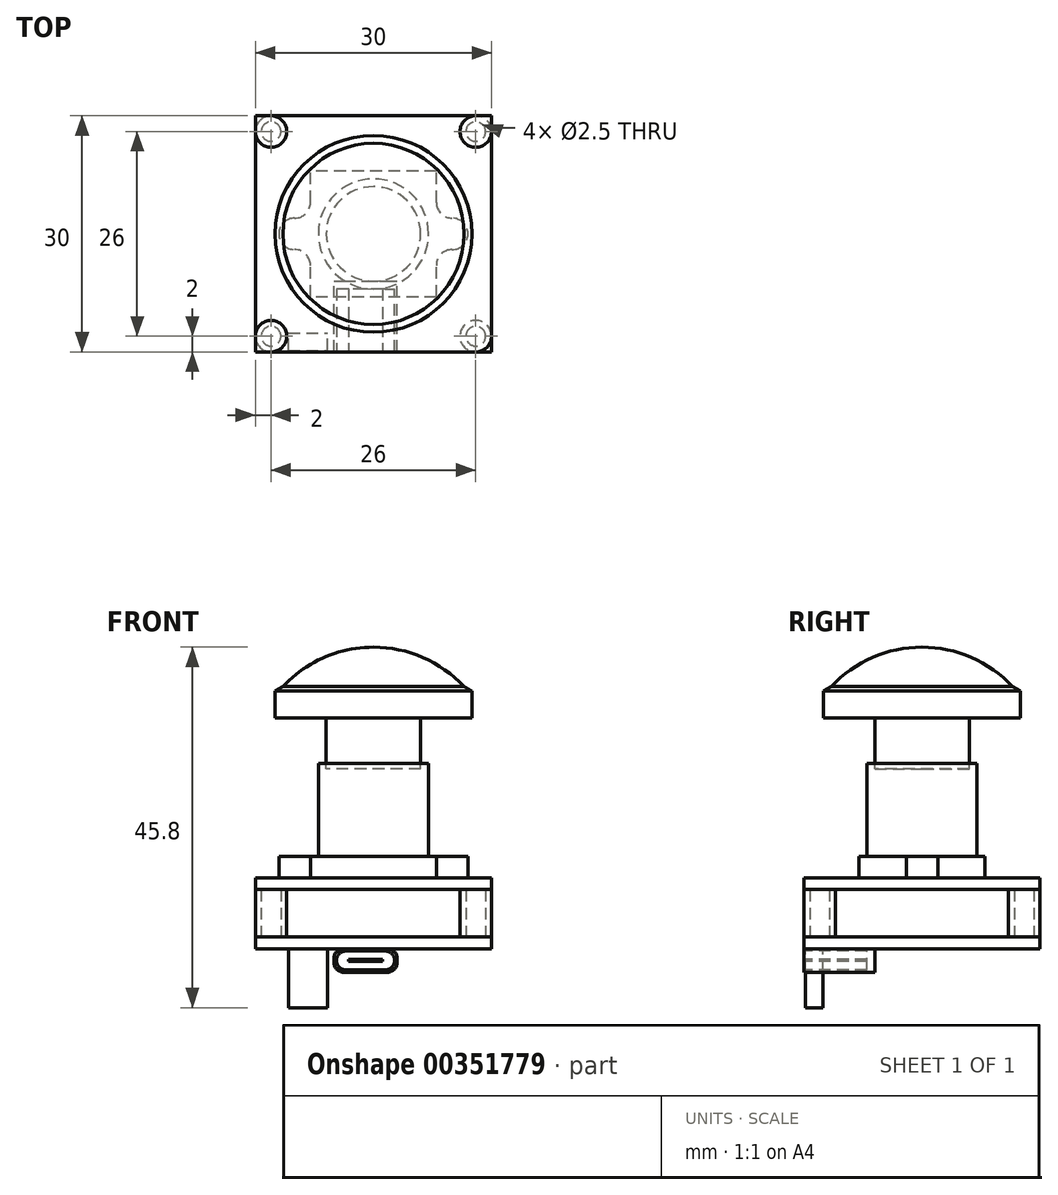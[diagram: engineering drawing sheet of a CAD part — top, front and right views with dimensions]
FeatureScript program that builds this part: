
annotation { "Feature Type Name" : "Feature", "Feature Type Description" : "" }
export const myFeature = defineFeature(function(context is Context, id is Id, definition is map)
    precondition{}
    {
        {
            var Q0;
            Q0=qCreatedBy(makeId("Top.planeOp"),FACE);
            var sketch = newSketch(context, id + "F0", { "sketchPlane" : qUnion([Q0])});
            skLineSegment(sketch, "E0.bottom", {"start": v(15, -15) * mm, "end": v(-15, -15) * mm});
            skLineSegment(sketch, "E0.top", {"start": v(15, 15) * mm, "end": v(-15, 15) * mm});
            skLineSegment(sketch, "E0.left", {"start": v(15, -15) * mm, "end": v(15, 15) * mm});
            skLineSegment(sketch, "E0.right", {"start": v(-15, -15) * mm, "end": v(-15, 15) * mm});
            skPoint(sketch, "E0.middle", {"position": v(0, 0) * mm});
            skSolve(sketch);
        }
        {
            var Q0;
            Q0=makeQuery(id+"F0.imprint","IMPRINT",FACE,{"disambiguationData":[TD([[makeQuery(id+"F0.imprint","IMPRINT",EDGE,{"derivedFrom":sQuery(id+"F0.wireOp",EDGE,"E0.bottom")}),-1.0]])]});
            extrude(context, id + "F1", {"entities" : qUnion([Q0]), "depth" : 1.5 * mm, "offsetDistance" : 25 * mm});
        }
        {
            var Q0;
            Q0=makeQuery(id+"F1.opExtrude","CAP_FACE",FACE,{"disambiguationData":[OSD([sQuery(id+"F0.wireOp",EDGE,"E0.bottom"),sQuery(id+"F0.wireOp",EDGE,"E0.top"),sQuery(id+"F0.wireOp",EDGE,"E0.left"),sQuery(id+"F0.wireOp",EDGE,"E0.right")])],"isStart":false});
            extrude(context, id + "F2", {"entities" : qUnion([Q0]), "operationType" : NewBodyOperationType.ADD, "depth" : 7.5 * mm, "offsetDistance" : 25 * mm, "hasSecondDirection" : true, "secondDirectionOppositeDirection" : false, "secondDirectionDepth" : 6 * mm});
        }
        {
            var Q0;
            Q0=makeQuery(id+"F1.opExtrude","CAP_FACE",FACE,{"disambiguationData":[OSD([sQuery(id+"F0.wireOp",EDGE,"E0.bottom"),sQuery(id+"F0.wireOp",EDGE,"E0.top"),sQuery(id+"F0.wireOp",EDGE,"E0.left"),sQuery(id+"F0.wireOp",EDGE,"E0.right")])],"isStart":false});
            var sketch = newSketch(context, id + "F3", { "sketchPlane" : qUnion([Q0])});
            skCircle(sketch, "E1", {"center": v(-13, 13) * mm, "radius": 1.25 * mm});
            skCircle(sketch, "E2", {"center": v(13, 13) * mm, "radius": 1.25 * mm});
            skCircle(sketch, "E3", {"center": v(-13, -13) * mm, "radius": 1.25 * mm});
            skCircle(sketch, "E4", {"center": v(13, 13) * mm, "radius": 2 * mm});
            skCircle(sketch, "E5", {"center": v(13, -13) * mm, "radius": 2 * mm});
            skCircle(sketch, "E6", {"center": v(-13, -13) * mm, "radius": 2 * mm});
            skCircle(sketch, "E7", {"center": v(-13, 13) * mm, "radius": 2 * mm});
            skCircle(sketch, "E8", {"center": v(13, -13) * mm, "radius": 1.25 * mm});
            skSolve(sketch);
        }
        {
            var Q0;
            Q0=makeQuery(id+"F3.imprint","IMPRINT",FACE,{"disambiguationData":[TD([[makeQuery(id+"F3.imprint","IMPRINT",EDGE,{"derivedFrom":sQuery(id+"F3.wireOp",EDGE,"E1")}),-1.0]])]});
            var Q1;
            Q1=makeQuery(id+"F3.imprint","IMPRINT",FACE,{"disambiguationData":[TD([[makeQuery(id+"F3.imprint","IMPRINT",EDGE,{"derivedFrom":sQuery(id+"F3.wireOp",EDGE,"E3")}),-1.0]])]});
            var Q2;
            Q2=makeQuery(id+"F3.imprint","IMPRINT",FACE,{"disambiguationData":[TD([[makeQuery(id+"F3.imprint","IMPRINT",EDGE,{"derivedFrom":sQuery(id+"F3.wireOp",EDGE,"E8")}),-1.0]])]});
            var Q3;
            Q3=makeQuery(id+"F3.imprint","IMPRINT",FACE,{"disambiguationData":[TD([[makeQuery(id+"F3.imprint","IMPRINT",EDGE,{"derivedFrom":sQuery(id+"F3.wireOp",EDGE,"E2")}),-1.0]])]});
            extrude(context, id + "F4", {"entities" : qUnion([Q0, Q1, Q2, Q3]), "depth" : 6 * mm, "offsetDistance" : 25 * mm});
        }
        {
            var Q0;
            Q0=makeQuery(id+"F2.opExtrude","CAP_FACE",FACE,{"disambiguationData":[OSD([sQuery(id+"F0.wireOp",EDGE,"E0.bottom"),sQuery(id+"F0.wireOp",EDGE,"E0.top"),sQuery(id+"F0.wireOp",EDGE,"E0.left"),sQuery(id+"F0.wireOp",EDGE,"E0.right")])],"isStart":false});
            var sketch = newSketch(context, id + "F5", { "sketchPlane" : qUnion([Q0])});
            skLineSegment(sketch, "E9.bottom", {"start": v(8, -8) * mm, "end": v(-8, -8) * mm});
            skLineSegment(sketch, "E9.top", {"start": v(8, 8) * mm, "end": v(-8, 8) * mm});
            skLineSegment(sketch, "E9.left", {"start": v(8, -8) * mm, "end": v(8, 8) * mm});
            skLineSegment(sketch, "E9.right", {"start": v(-8, -8) * mm, "end": v(-8, 8) * mm});
            skPoint(sketch, "E9.middle", {"position": v(0, 0) * mm});
            skLineSegment(sketch, "E10.bottom", {"start": v(-8, -2) * mm, "end": v(-12, -2) * mm});
            skLineSegment(sketch, "E10.top", {"start": v(-8, 2) * mm, "end": v(-12, 2) * mm});
            skLineSegment(sketch, "E10.left", {"start": v(-8, -2) * mm, "end": v(-8, 2) * mm});
            skLineSegment(sketch, "E10.right", {"start": v(-12, -2) * mm, "end": v(-12, 2) * mm});
            skPoint(sketch, "E10.middle", {"position": v(-10, 0) * mm});
            skPoint(sketch, "E10.middle.positionSnap0", {"position": v(-8, 0) * mm});
            skPoint(sketch, "E10.centerSnap0", {"position": v(-8, 0) * mm});
            skLineSegment(sketch, "E11.bottom", {"start": v(8, -2) * mm, "end": v(12, -2) * mm});
            skLineSegment(sketch, "E11.top", {"start": v(8, 2) * mm, "end": v(12, 2) * mm});
            skLineSegment(sketch, "E11.left", {"start": v(8, -2) * mm, "end": v(8, 2) * mm});
            skLineSegment(sketch, "E11.right", {"start": v(12, -2) * mm, "end": v(12, 2) * mm});
            skPoint(sketch, "E11.middle", {"position": v(10, 0) * mm});
            skCircle(sketch, "E12", {"center": v(0, 0) * mm, "radius": 7 * mm});
            skSolve(sketch);
        }
        {
            var Q0;
            Q0=makeQuery(id+"F5.imprint","IMPRINT",FACE,{"disambiguationData":[TD([[makeQuery(id+"F5.imprint","IMPRINT",EDGE,{"derivedFrom":sQuery(id+"F5.wireOp",EDGE,"E10.bottom")}),-1.0]])]});
            var Q1;
            {var subQ3=sQuery(id+"F5.wireOp",EDGE,"E9.bottom");Q1=makeQuery(id+"F5.imprint","IMPRINT",FACE,{"disambiguationData":[TD([[makeQuery(id+"F5.imprint","IMPRINT",EDGE,{"derivedFrom":subQ3}),-1.0]])]});}
            var Q2;
            Q2=makeQuery(id+"F5.imprint","IMPRINT",FACE,{"disambiguationData":[TD([[makeQuery(id+"F5.imprint","IMPRINT",EDGE,{"derivedFrom":sQuery(id+"F5.wireOp",EDGE,"E11.bottom")}),1.0]])]});
            var Q3;
            Q3=makeQuery(id+"F5.imprint","IMPRINT",FACE,{"disambiguationData":[TD([[makeQuery(id+"F5.imprint","IMPRINT",EDGE,{"derivedFrom":sQuery(id+"F5.wireOp",EDGE,"E12")}),1.0]])]});
            extrude(context, id + "F6", {"entities" : qUnion([Q0, Q1, Q2, Q3]), "depth" : 2.7 * mm, "offsetDistance" : 25 * mm});
        }
        {
            var Q0;
            Q0=makeQuery(id+"F6.opExtrude","SWEPT_EDGE",EDGE,{"disambiguationData":[OSD([sQuery(id+"F5.wireOp",EDGE,"E10.top"),sQuery(id+"F5.wireOp",EDGE,"E10.right")])]});
            var Q1;
            Q1=makeQuery(id+"F6.opExtrude","SWEPT_EDGE",EDGE,{"disambiguationData":[OSD([sQuery(id+"F5.wireOp",EDGE,"E10.bottom"),sQuery(id+"F5.wireOp",EDGE,"E10.right")])]});
            var Q2;
            Q2=makeQuery(id+"F6.opExtrude","SWEPT_EDGE",EDGE,{"disambiguationData":[OSD([sQuery(id+"F5.wireOp",EDGE,"E9.right"),sQuery(id+"F5.wireOp",EDGE,"E10.top"),sQuery(id+"F5.wireOp",EDGE,"E10.left")])]});
            var Q3;
            Q3=makeQuery(id+"F6.opExtrude","SWEPT_EDGE",EDGE,{"disambiguationData":[OSD([sQuery(id+"F5.wireOp",EDGE,"E9.right"),sQuery(id+"F5.wireOp",EDGE,"E10.bottom"),sQuery(id+"F5.wireOp",EDGE,"E10.left")])]});
            var Q4;
            Q4=makeQuery(id+"F6.opExtrude","SWEPT_EDGE",EDGE,{"disambiguationData":[OSD([sQuery(id+"F5.wireOp",EDGE,"E11.bottom"),sQuery(id+"F5.wireOp",EDGE,"E11.right")])]});
            var Q5;
            Q5=makeQuery(id+"F6.opExtrude","SWEPT_EDGE",EDGE,{"disambiguationData":[OSD([sQuery(id+"F5.wireOp",EDGE,"E9.left"),sQuery(id+"F5.wireOp",EDGE,"E11.bottom"),sQuery(id+"F5.wireOp",EDGE,"E11.left")])]});
            var Q6;
            Q6=makeQuery(id+"F6.opExtrude","SWEPT_EDGE",EDGE,{"disambiguationData":[OSD([sQuery(id+"F5.wireOp",EDGE,"E9.left"),sQuery(id+"F5.wireOp",EDGE,"E11.top"),sQuery(id+"F5.wireOp",EDGE,"E11.left")])]});
            var Q7;
            Q7=makeQuery(id+"F6.opExtrude","SWEPT_EDGE",EDGE,{"disambiguationData":[OSD([sQuery(id+"F5.wireOp",EDGE,"E11.top"),sQuery(id+"F5.wireOp",EDGE,"E11.right")])]});
            fillet(context, id + "F7", {"entities" : qUnion([Q0, Q1, Q2, Q3, Q4, Q5, Q6, Q7]), "radius" : 2 * mm, "tangentPropagation" : true, "allowEdgeOverflow" : false});
        }
        {
            var Q0;
            Q0=makeQuery(id+"F5.imprint","IMPRINT",FACE,{"disambiguationData":[TD([[makeQuery(id+"F5.imprint","IMPRINT",EDGE,{"derivedFrom":sQuery(id+"F5.wireOp",EDGE,"E12")}),1.0]])]});
            extrude(context, id + "F8", {"entities" : qUnion([Q0]), "operationType" : NewBodyOperationType.ADD, "depth" : 14.5 * mm, "offsetDistance" : 25 * mm});
        }
        {
            var Q0;
            Q0=qCreatedBy(makeId("Front.planeOp"),FACE);
            var sketch = newSketch(context, id + "F9", { "sketchPlane" : qUnion([Q0])});
            skLineSegment(sketch, "E13.bottom", {"start": v(0, 27.8) * mm, "end": v(-6, 27.8) * mm});
            skLineSegment(sketch, "E13.top", {"start": v(0, 22.8) * mm, "end": v(-6, 22.8) * mm});
            skLineSegment(sketch, "E13.left", {"start": v(0, 27.8) * mm, "end": v(0, 22.8) * mm});
            skLineSegment(sketch, "E13.right", {"start": v(-6, 27.8) * mm, "end": v(-6, 22.8) * mm});
            skLineSegment(sketch, "E14.top", {"start": v(0, 29.3) * mm, "end": v(-6, 29.3) * mm});
            skLineSegment(sketch, "E14.left", {"start": v(0, 27.8) * mm, "end": v(0, 29.3) * mm});
            skLineSegment(sketch, "E14.right", {"start": v(-6, 27.8) * mm, "end": v(-6, 29.3) * mm});
            skLineSegment(sketch, "E15.bottom", {"start": v(0, 29.3) * mm, "end": v(-12.5, 29.3) * mm});
            skLineSegment(sketch, "E15.top", {"start": v(0, 33.3) * mm, "end": v(-11.5, 33.3) * mm});
            skLineSegment(sketch, "E15.left", {"start": v(0, 29.3) * mm, "end": v(0, 33.3) * mm});
            skLineSegment(sketch, "E15.right", {"start": v(-12.5, 29.3) * mm, "end": v(-12.5, 32.72) * mm});
            skLineSegment(sketch, "E16", {"start": v(-12.5, 32.72) * mm, "end": v(-11.5, 33.3) * mm});
            skArc(sketch, "E17", {"start": v(-11.5, 33.3) * mm, "mid": v(-6.27, 37) * mm, "end": v(0, 38.3) * mm});
            skLineSegment(sketch, "E18", {"start": v(0, 38.3) * mm, "end": v(0, 33.3) * mm});
            skSolve(sketch);
        }
        {
            var Q0;
            Q0=makeQuery(id+"F9.imprint","IMPRINT",FACE,{"disambiguationData":[TD([[makeQuery(id+"F9.imprint","IMPRINT",EDGE,{"derivedFrom":sQuery(id+"F9.wireOp",EDGE,"E15.top")}),-1.0]])]});
            var Q1;
            Q1=sQuery(id+"F9.wireOp",EDGE,"E13.left");
            revolve(context, id + "F10", {"surfaceOperationType" : NewSurfaceOperationType.NEW, "entities" : qUnion([Q0]), "axis" : qUnion([Q1]), "revolveType" : RevolveType.FULL});
        }
        {
            var Q0;
            Q0=makeQuery(id+"F9.imprint","IMPRINT",FACE,{"disambiguationData":[TD([[makeQuery(id+"F9.imprint","IMPRINT",EDGE,{"derivedFrom":sQuery(id+"F9.wireOp",EDGE,"E15.top")}),1.0]])]});
            var Q1;
            {var subQ1=sQuery(id+"F9.wireOp",EDGE,"E14.left");Q1=makeQuery(id+"F9.imprint","IMPRINT",FACE,{"disambiguationData":[TD([[makeQuery(id+"F9.imprint","IMPRINT",EDGE,{"derivedFrom":subQ1}),1.0]])]});}
            var Q2;
            Q2=makeQuery(id+"F9.imprint","IMPRINT",FACE,{"disambiguationData":[TD([[makeQuery(id+"F9.imprint","IMPRINT",EDGE,{"derivedFrom":sQuery(id+"F9.wireOp",EDGE,"E13.top")}),-1.0]])]});
            var Q3;
            Q3=sQuery(id+"F9.wireOp",EDGE,"E13.left");
            revolve(context, id + "F11", {"surfaceOperationType" : NewSurfaceOperationType.NEW, "entities" : qUnion([Q0, Q1, Q2]), "axis" : qUnion([Q3]), "revolveType" : RevolveType.FULL});
        }
        {
            var Q0;
            Q0=makeQuery(id+"F1.opExtrude","CAP_FACE",FACE,{"disambiguationData":[OSD([sQuery(id+"F0.wireOp",EDGE,"E0.bottom"),sQuery(id+"F0.wireOp",EDGE,"E0.top"),sQuery(id+"F0.wireOp",EDGE,"E0.left"),sQuery(id+"F0.wireOp",EDGE,"E0.right")])],"isStart":true});
            var sketch = newSketch(context, id + "F12", { "sketchPlane" : qUnion([Q0])});
            skLineSegment(sketch, "E19.bottom", {"start": v(-5, 15) * mm, "end": v(3, 15) * mm});
            skLineSegment(sketch, "E19.top", {"start": v(-5, 6) * mm, "end": v(3, 6) * mm});
            skLineSegment(sketch, "E19.left", {"start": v(-5, 15) * mm, "end": v(-5, 6) * mm});
            skLineSegment(sketch, "E19.right", {"start": v(3, 15) * mm, "end": v(3, 6) * mm});
            skSolve(sketch);
        }
        {
            var Q0;
            Q0=makeQuery(id+"F12.imprint","IMPRINT",FACE,{"disambiguationData":[TD([[makeQuery(id+"F12.imprint","IMPRINT",EDGE,{"derivedFrom":sQuery(id+"F12.wireOp",EDGE,"E19.bottom")}),1.0]])]});
            extrude(context, id + "F13", {"entities" : qUnion([Q0]), "depth" : 3 * mm, "offsetDistance" : 25 * mm});
        }
        {
            var Q0;
            Q0=makeQuery(id+"F13.opExtrude","SWEPT_FACE",FACE,{"disambiguationData":[OSD([sQuery(id+"F12.wireOp",EDGE,"E19.bottom")])]});
            var sketch = newSketch(context, id + "F14", { "sketchPlane" : qUnion([Q0])});
            skLineSegment(sketch, "E20.0", {"start": v(2.7, -2.7) * mm, "end": v(2.7, -0.3) * mm});
            skLineSegment(sketch, "E20.1", {"start": v(2.7, -2.7) * mm, "end": v(-4.7, -2.7) * mm});
            skLineSegment(sketch, "E20.2", {"start": v(-4.7, -2.7) * mm, "end": v(-4.7, -0.3) * mm});
            skLineSegment(sketch, "E20.3", {"start": v(2.7, -0.3) * mm, "end": v(-4.7, -0.3) * mm});
            skPoint(sketch, "E21.top.end.orphan", {"position": v(1.8, -1.8) * mm});
            skLineSegment(sketch, "E22.bottom", {"start": v(1.18, -1.65) * mm, "end": v(-3.18, -1.65) * mm});
            skLineSegment(sketch, "E22.top", {"start": v(1.18, -1.35) * mm, "end": v(-3.18, -1.35) * mm});
            skLineSegment(sketch, "E22.left", {"start": v(1.18, -1.65) * mm, "end": v(1.18, -1.35) * mm});
            skLineSegment(sketch, "E22.right", {"start": v(-3.18, -1.65) * mm, "end": v(-3.18, -1.35) * mm});
            skPoint(sketch, "E22.middle", {"position": v(-1, -1.5) * mm});
            skPoint(sketch, "E22.middle.positionSnap0", {"position": v(3, -1.5) * mm});
            skPoint(sketch, "E22.middle.positionSnap1", {"position": v(-1, 0) * mm});
            skPoint(sketch, "E22.centerSnap0", {"position": v(3, -1.5) * mm});
            skPoint(sketch, "E22.centerSnap1", {"position": v(-1, 0) * mm});
            skSolve(sketch);
        }
        {
            var Q0;
            Q0=makeQuery(id+"F14.imprint","IMPRINT",FACE,{"disambiguationData":[TD([[makeQuery(id+"F14.imprint","IMPRINT",EDGE,{"derivedFrom":sQuery(id+"F14.wireOp",EDGE,"E20.0")}),1.0]])]});
            extrude(context, id + "F15", {"entities" : qUnion([Q0]), "operationType" : NewBodyOperationType.REMOVE, "oppositeDirection" : true, "depth" : 8 * mm, "offsetDistance" : 25 * mm});
        }
        {
            var Q0;
            Q0=makeQuery(id+"F13.opExtrude","CAP_EDGE",EDGE,{"disambiguationData":[OSD([sQuery(id+"F12.wireOp",EDGE,"E19.left")])],"isStart":false});
            var Q1;
            Q1=makeQuery(id+"F13.opExtrude","CAP_EDGE",EDGE,{"disambiguationData":[OSD([sQuery(id+"F12.wireOp",EDGE,"E19.left")])],"isStart":true});
            var Q2;
            Q2=makeQuery(id+"F13.opExtrude","CAP_EDGE",EDGE,{"disambiguationData":[OSD([sQuery(id+"F12.wireOp",EDGE,"E19.right")])],"isStart":true});
            var Q3;
            Q3=makeQuery(id+"F13.opExtrude","CAP_EDGE",EDGE,{"disambiguationData":[OSD([sQuery(id+"F12.wireOp",EDGE,"E19.right")])],"isStart":false});
            var Q4;
            Q4=makeQuery(id+"F15.boolean.opBoolean","COPY",EDGE,{"derivedFrom":makeQuery(id+"F15.opExtrude","SWEPT_EDGE",EDGE,{"disambiguationData":[OSD([sQuery(id+"F14.wireOp",EDGE,"E20.2"),sQuery(id+"F14.wireOp",EDGE,"E20.3")])]})});
            var Q5;
            Q5=makeQuery(id+"F15.boolean.opBoolean","COPY",EDGE,{"derivedFrom":makeQuery(id+"F15.opExtrude","SWEPT_EDGE",EDGE,{"disambiguationData":[OSD([sQuery(id+"F14.wireOp",EDGE,"E20.0"),sQuery(id+"F14.wireOp",EDGE,"E20.3")])]})});
            var Q6;
            Q6=makeQuery(id+"F15.boolean.opBoolean","COPY",EDGE,{"derivedFrom":makeQuery(id+"F15.opExtrude","SWEPT_EDGE",EDGE,{"disambiguationData":[OSD([sQuery(id+"F14.wireOp",EDGE,"E20.0"),sQuery(id+"F14.wireOp",EDGE,"E20.1")])]})});
            var Q7;
            Q7=makeQuery(id+"F15.boolean.opBoolean","COPY",EDGE,{"derivedFrom":makeQuery(id+"F15.opExtrude","SWEPT_EDGE",EDGE,{"disambiguationData":[OSD([sQuery(id+"F14.wireOp",EDGE,"E20.1"),sQuery(id+"F14.wireOp",EDGE,"E20.2")])]})});
            fillet(context, id + "F16", {"entities" : qUnion([Q0, Q1, Q2, Q3, Q4, Q5, Q6, Q7]), "radius" : 1.2 * mm, "tangentPropagation" : true, "allowEdgeOverflow" : false});
        }
        {
            var Q0;
            Q0=makeQuery(id+"F1.opExtrude","CAP_FACE",FACE,{"disambiguationData":[OSD([sQuery(id+"F0.wireOp",EDGE,"E0.bottom"),sQuery(id+"F0.wireOp",EDGE,"E0.top"),sQuery(id+"F0.wireOp",EDGE,"E0.left"),sQuery(id+"F0.wireOp",EDGE,"E0.right")])],"isStart":true});
            var sketch = newSketch(context, id + "F17", { "sketchPlane" : qUnion([Q0])});
            skLineSegment(sketch, "E23.bottom", {"start": v(-10.8, 14.8) * mm, "end": v(-5.8, 14.8) * mm});
            skLineSegment(sketch, "E23.top", {"start": v(-10.8, 12.6) * mm, "end": v(-5.8, 12.6) * mm});
            skLineSegment(sketch, "E23.left", {"start": v(-10.8, 14.8) * mm, "end": v(-10.8, 12.6) * mm});
            skLineSegment(sketch, "E23.right", {"start": v(-5.8, 14.8) * mm, "end": v(-5.8, 12.6) * mm});
            skSolve(sketch);
        }
        {
            var Q0;
            Q0=makeQuery(id+"F17.imprint","IMPRINT",FACE,{"disambiguationData":[TD([[makeQuery(id+"F17.imprint","IMPRINT",EDGE,{"derivedFrom":sQuery(id+"F17.wireOp",EDGE,"E23.bottom")}),-1.0]])]});
            extrude(context, id + "F18", {"entities" : qUnion([Q0]), "depth" : 7.5 * mm, "offsetDistance" : 25 * mm});
        }
    });
